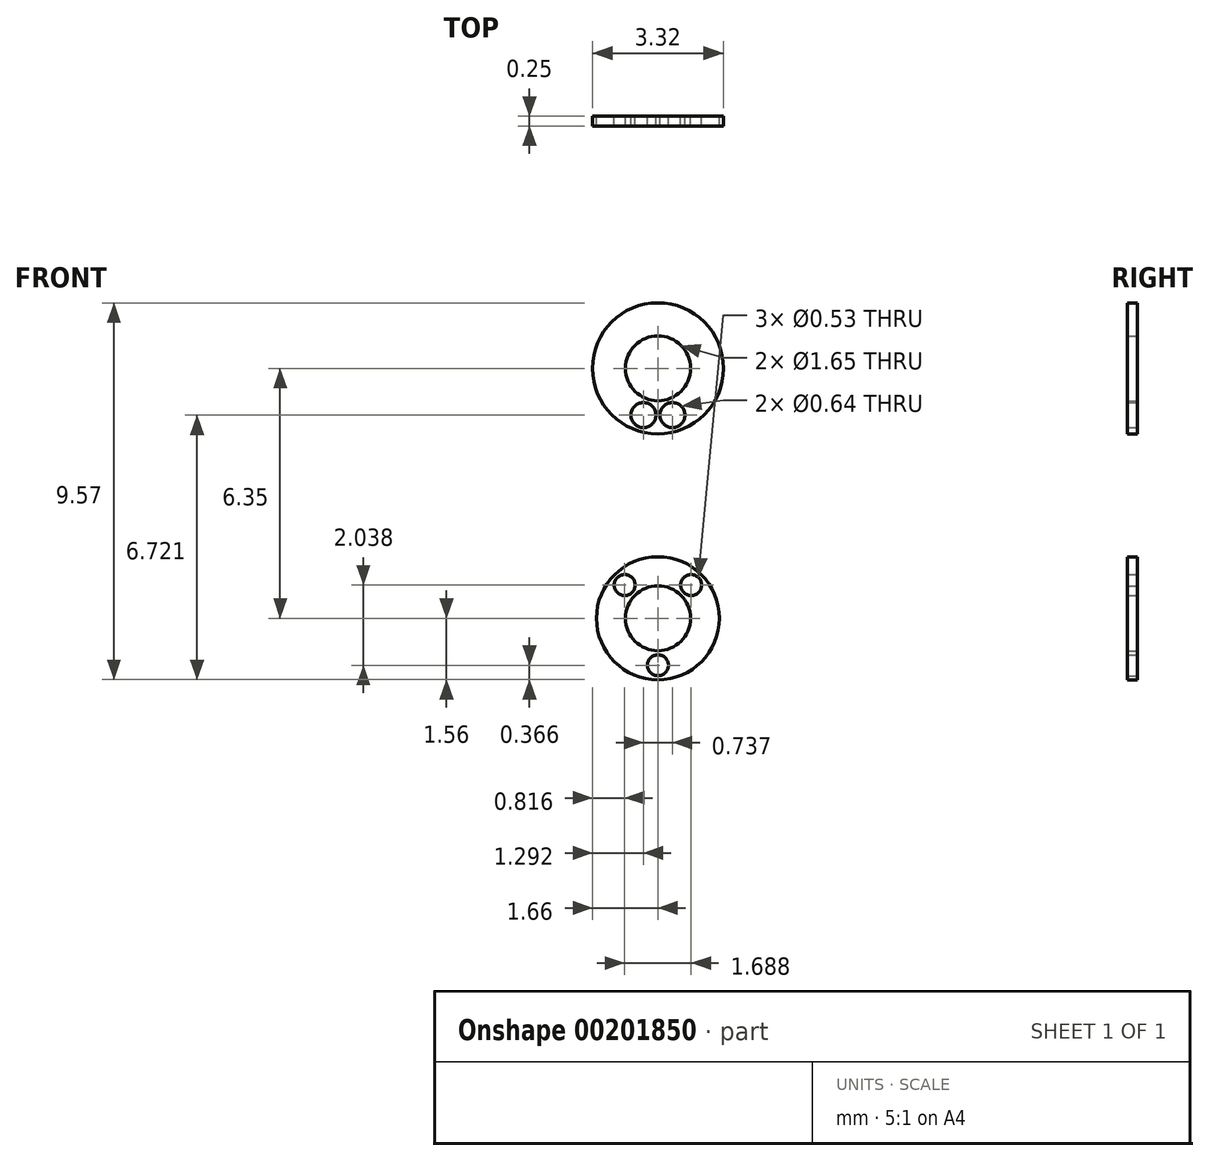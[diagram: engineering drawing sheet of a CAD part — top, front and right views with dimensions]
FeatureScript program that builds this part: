
annotation { "Feature Type Name" : "Feature", "Feature Type Description" : "" }
export const myFeature = defineFeature(function(context is Context, id is Id, definition is map)
    precondition{}
    {
        {
            var Q0;
            Q0=qCreatedBy(makeId("Front.planeOp"),FACE);
            var sketch = newSketch(context, id + "F0", { "sketchPlane" : qUnion([Q0])});
            skCircle(sketch, "E0", {"center": v(0, 0) * mm, "radius": 1.66 * mm});
            skCircle(sketch, "E1", {"center": v(0, 0) * mm, "radius": 0.83 * mm});
            skCircle(sketch, "E2", {"center": v(0.37, -1.19) * mm, "radius": 0.32 * mm});
            skCircle(sketch, "E3.MirrorC", {"center": v(-0.37, -1.19) * mm, "radius": 0.32 * mm});
            skCircle(sketch, "E4", {"center": v(0, -6.35) * mm, "radius": 0.83 * mm});
            skCircle(sketch, "E5", {"center": v(0.84, -5.5) * mm, "radius": 0.27 * mm});
            skCircle(sketch, "E6", {"center": v(0, -6.35) * mm, "radius": 1.56 * mm});
            skCircle(sketch, "E7", {"center": v(0, -7.54) * mm, "radius": 0.27 * mm});
            skCircle(sketch, "E8.MirrorC", {"center": v(-0.84, -5.5) * mm, "radius": 0.27 * mm});
            skLineSegment(sketch, "E9", {"start": v(0, -6.35) * mm, "end": v(0.84, -5.5) * mm, "construction": true});
            skSolve(sketch);
        }
        {
            var Q0;
            Q0=makeQuery(id+"F0.imprint","IMPRINT",FACE,{"disambiguationData":[TD([[makeQuery(id+"F0.imprint","IMPRINT",EDGE,{"derivedFrom":sQuery(id+"F0.wireOp",EDGE,"E0")}),1.0]])]});
            var Q1;
            Q1=makeQuery(id+"F0.imprint","IMPRINT",FACE,{"disambiguationData":[TD([[makeQuery(id+"F0.imprint","IMPRINT",EDGE,{"derivedFrom":sQuery(id+"F0.wireOp",EDGE,"E4")}),-1.0]])]});
            extrude(context, id + "F1", {"entities" : qUnion([Q0, Q1]), "depth" : 0.25 * mm});
        }
    });
